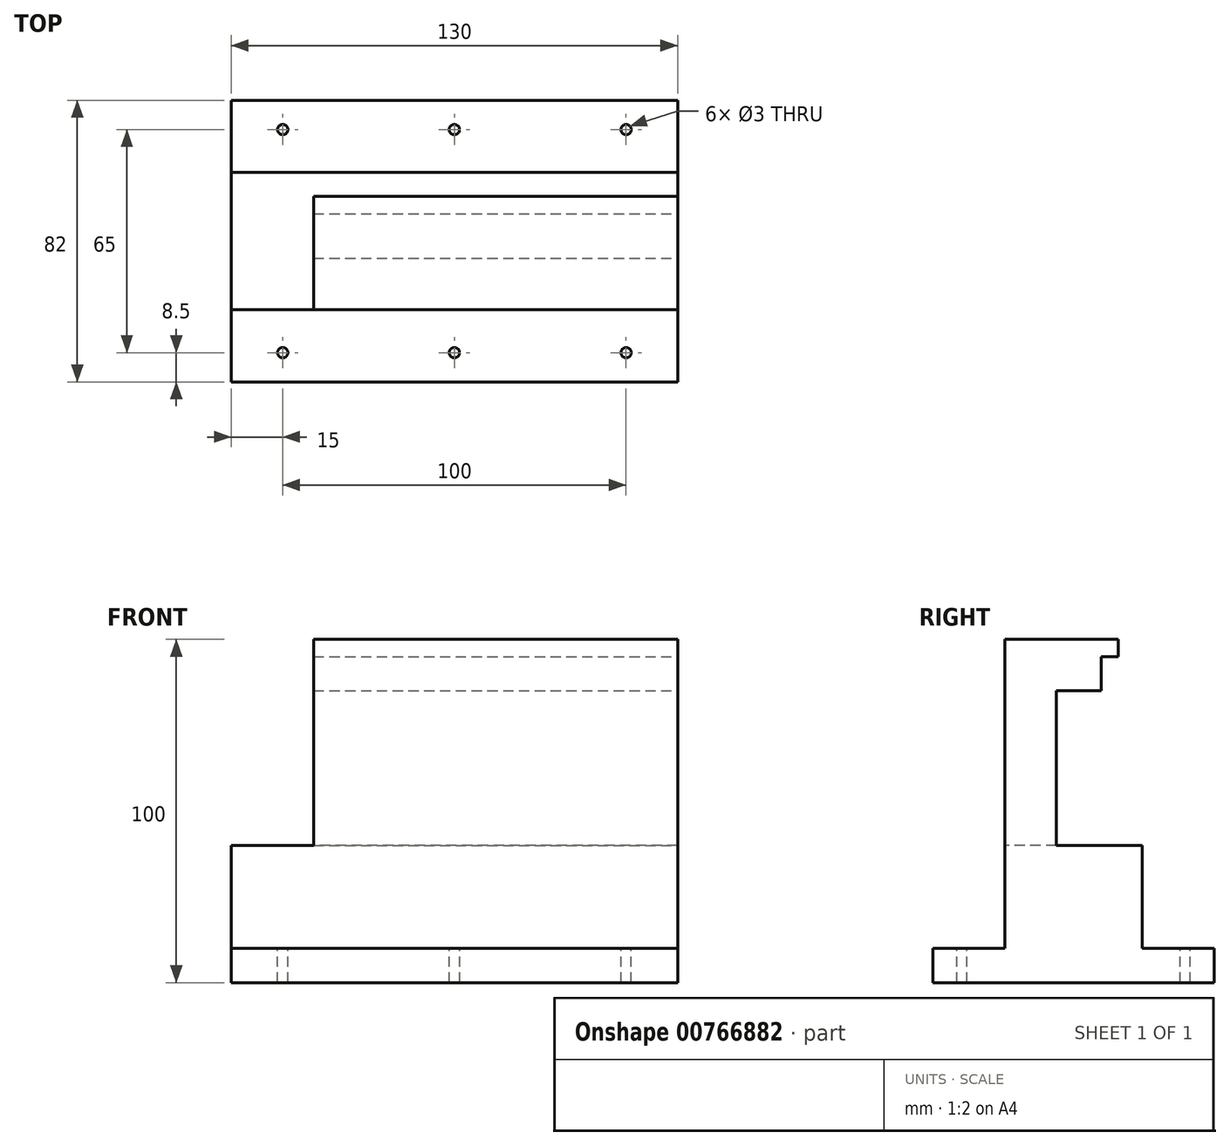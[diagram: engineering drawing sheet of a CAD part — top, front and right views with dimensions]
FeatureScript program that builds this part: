
annotation { "Feature Type Name" : "Feature", "Feature Type Description" : "" }
export const myFeature = defineFeature(function(context is Context, id is Id, definition is map)
    precondition{}
    {
        {
            var Q0;
            Q0=qCreatedBy(makeId("Right.planeOp"),FACE);
            var sketch = newSketch(context, id + "F0", { "sketchPlane" : qUnion([Q0])});
            skLineSegment(sketch, "E0", {"start": v(0, 0) * mm, "end": v(82, 0) * mm});
            skLineSegment(sketch, "E1", {"start": v(82, 0) * mm, "end": v(82, 10) * mm});
            skLineSegment(sketch, "E2", {"start": v(82, 10) * mm, "end": v(61, 10) * mm});
            skLineSegment(sketch, "E3", {"start": v(61, 10) * mm, "end": v(61, 40) * mm});
            skLineSegment(sketch, "E4", {"start": v(61, 40) * mm, "end": v(21, 40) * mm});
            skLineSegment(sketch, "E5", {"start": v(21, 40) * mm, "end": v(21, 10) * mm});
            skLineSegment(sketch, "E6", {"start": v(21, 10) * mm, "end": v(0, 10) * mm});
            skLineSegment(sketch, "E7", {"start": v(0, 0) * mm, "end": v(0, 10) * mm});
            skSolve(sketch);
        }
        {
            var Q0;
            Q0=makeQuery(id+"F0.imprint","IMPRINT",FACE,{"disambiguationData":[TD([[makeQuery(id+"F0.imprint","IMPRINT",EDGE,{"derivedFrom":sQuery(id+"F0.wireOp",EDGE,"E0")}),1.0]])]});
            extrude(context, id + "F1", {"entities" : qUnion([Q0]), "depth" : 65 * mm, "offsetDistance" : 25 * mm, "hasSecondDirection" : true, "secondDirectionOppositeDirection" : true, "secondDirectionDepth" : 65 * mm});
        }
        {
            var Q0;
            Q0=makeQuery(id+"F1.opExtrude","CAP_FACE",FACE,{"disambiguationData":[OSD([sQuery(id+"F0.wireOp",EDGE,"E0"),sQuery(id+"F0.wireOp",EDGE,"E1"),sQuery(id+"F0.wireOp",EDGE,"E2"),sQuery(id+"F0.wireOp",EDGE,"E3"),sQuery(id+"F0.wireOp",EDGE,"E4"),sQuery(id+"F0.wireOp",EDGE,"E5"),sQuery(id+"F0.wireOp",EDGE,"E6"),sQuery(id+"F0.wireOp",EDGE,"E7")])],"isStart":false});
            var sketch = newSketch(context, id + "F2", { "sketchPlane" : qUnion([Q0])});
            skLineSegment(sketch, "E8", {"start": v(21, 40) * mm, "end": v(21, 100) * mm});
            skLineSegment(sketch, "E9", {"start": v(21, 100) * mm, "end": v(54, 100) * mm});
            skLineSegment(sketch, "E10", {"start": v(54, 100) * mm, "end": v(54, 95) * mm});
            skLineSegment(sketch, "E11", {"start": v(54, 95) * mm, "end": v(49, 95) * mm});
            skLineSegment(sketch, "E12", {"start": v(49, 95) * mm, "end": v(49, 85) * mm});
            skLineSegment(sketch, "E13", {"start": v(49, 85) * mm, "end": v(36, 85) * mm});
            skLineSegment(sketch, "E14", {"start": v(36, 85) * mm, "end": v(36, 40) * mm});
            skLineSegment(sketch, "E15", {"start": v(36, 40) * mm, "end": v(21, 40) * mm});
            skSolve(sketch);
        }
        {
            var Q0;
            Q0=makeQuery(id+"F2.imprint","IMPRINT",FACE,{"disambiguationData":[TD([[makeQuery(id+"F2.imprint","IMPRINT",EDGE,{"derivedFrom":sQuery(id+"F2.wireOp",EDGE,"E8")}),-1.0]])]});
            extrude(context, id + "F3", {"entities" : qUnion([Q0]), "operationType" : NewBodyOperationType.ADD, "oppositeDirection" : true, "depth" : 106 * mm, "offsetDistance" : 25 * mm});
        }
        {
            var Q0;
            Q0=makeQuery(id+"F1.opExtrude","SWEPT_FACE",FACE,{"disambiguationData":[OSD([sQuery(id+"F0.wireOp",EDGE,"E2")])]});
            var sketch = newSketch(context, id + "F4", { "sketchPlane" : qUnion([Q0])});
            skCircle(sketch, "E16", {"center": v(-50, 73.5) * mm, "radius": 1.5 * mm});
            skCircle(sketch, "E17", {"center": v(0, 73.5) * mm, "radius": 1.5 * mm});
            skCircle(sketch, "E18", {"center": v(50, 73.5) * mm, "radius": 1.5 * mm});
            skCircle(sketch, "E19", {"center": v(50, 8.5) * mm, "radius": 1.5 * mm});
            skCircle(sketch, "E20", {"center": v(0, 8.5) * mm, "radius": 1.5 * mm});
            skCircle(sketch, "E21", {"center": v(-50, 8.5) * mm, "radius": 1.5 * mm});
            skSolve(sketch);
        }
        {
            var Q0;
            Q0=makeQuery(id+"F4.imprint","IMPRINT",FACE,{"disambiguationData":[TD([[makeQuery(id+"F4.imprint","IMPRINT",EDGE,{"derivedFrom":sQuery(id+"F4.wireOp",EDGE,"E16")}),1.0]])]});
            var Q1;
            Q1=makeQuery(id+"F4.imprint","IMPRINT",FACE,{"disambiguationData":[TD([[makeQuery(id+"F4.imprint","IMPRINT",EDGE,{"derivedFrom":sQuery(id+"F4.wireOp",EDGE,"E17")}),1.0]])]});
            var Q2;
            Q2=makeQuery(id+"F4.imprint","IMPRINT",FACE,{"disambiguationData":[TD([[makeQuery(id+"F4.imprint","IMPRINT",EDGE,{"derivedFrom":sQuery(id+"F4.wireOp",EDGE,"E18")}),1.0]])]});
            var Q3;
            Q3=makeQuery(id+"F4.imprint","IMPRINT",FACE,{"disambiguationData":[TD([[makeQuery(id+"F4.imprint","IMPRINT",EDGE,{"derivedFrom":sQuery(id+"F4.wireOp",EDGE,"E19")}),1.0]])]});
            var Q4;
            Q4=makeQuery(id+"F4.imprint","IMPRINT",FACE,{"disambiguationData":[TD([[makeQuery(id+"F4.imprint","IMPRINT",EDGE,{"derivedFrom":sQuery(id+"F4.wireOp",EDGE,"E20")}),1.0]])]});
            var Q5;
            Q5=makeQuery(id+"F4.imprint","IMPRINT",FACE,{"disambiguationData":[TD([[makeQuery(id+"F4.imprint","IMPRINT",EDGE,{"derivedFrom":sQuery(id+"F4.wireOp",EDGE,"E21")}),1.0]])]});
            extrude(context, id + "F5", {"entities" : qUnion([Q0, Q1, Q2, Q3, Q4, Q5]), "operationType" : NewBodyOperationType.REMOVE, "oppositeDirection" : true, "depth" : 10 * mm, "offsetDistance" : 25 * mm});
        }
    });
